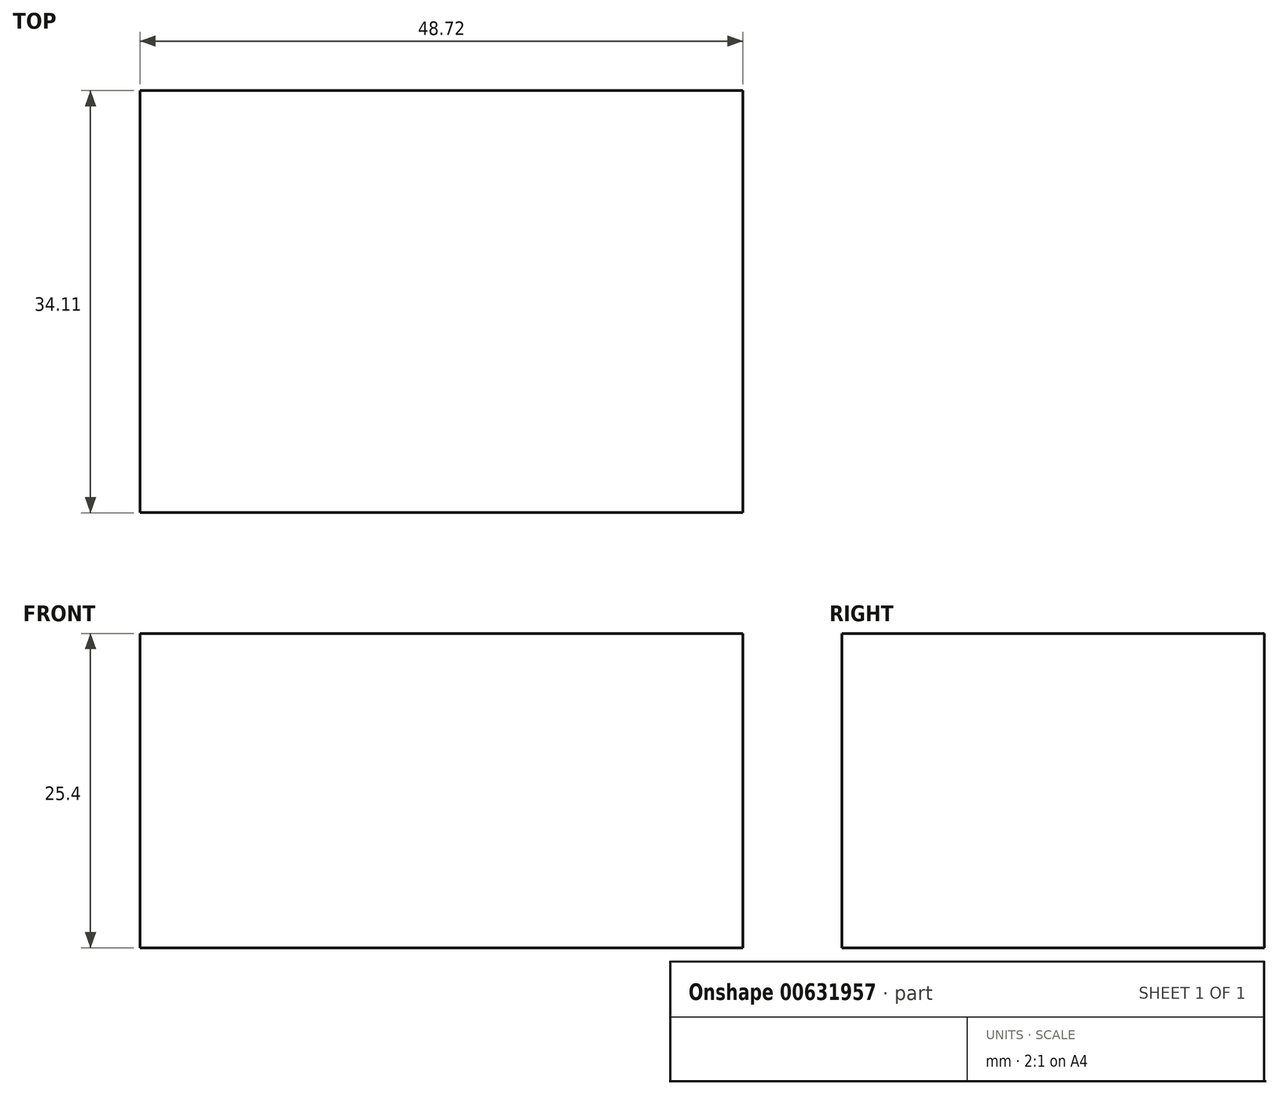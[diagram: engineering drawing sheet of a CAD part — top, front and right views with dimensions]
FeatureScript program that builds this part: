
annotation { "Feature Type Name" : "Feature", "Feature Type Description" : "" }
export const myFeature = defineFeature(function(context is Context, id is Id, definition is map)
    precondition{}
    {
        {
            var Q0;
            Q0=qCreatedBy(makeId("Top.planeOp"),FACE);
            var sketch = newSketch(context, id + "F0", { "sketchPlane" : qUnion([Q0])});
            skLineSegment(sketch, "E0.bottom", {"start": v(-12.86, 21.65) * mm, "end": v(-61.58, 21.65) * mm});
            skLineSegment(sketch, "E0.top", {"start": v(-12.86, 55.76) * mm, "end": v(-61.58, 55.76) * mm});
            skLineSegment(sketch, "E0.left", {"start": v(-12.86, 21.65) * mm, "end": v(-12.86, 55.76) * mm});
            skLineSegment(sketch, "E0.right", {"start": v(-61.58, 21.65) * mm, "end": v(-61.58, 55.76) * mm});
            skPoint(sketch, "E0.middle", {"position": v(-37.22, 38.7) * mm});
            skLineSegment(sketch, "E1.bottom", {"start": v(-42.09, 21.65) * mm, "end": v(16.38, 21.65) * mm});
            skLineSegment(sketch, "E1.top", {"start": v(-42.09, 21.65) * mm, "end": v(16.38, 21.65) * mm});
            skLineSegment(sketch, "E1.left", {"start": v(-42.09, 21.65) * mm, "end": v(-42.09, 21.65) * mm});
            skLineSegment(sketch, "E1.right", {"start": v(16.38, 21.65) * mm, "end": v(16.38, 21.65) * mm});
            skPoint(sketch, "E1.middle", {"position": v(-12.86, 21.65) * mm});
            skSolve(sketch);
        }
        {
            var Q0;
            Q0 = qSketchRegion(id + "F0", true);
            extrude(context, id + "F1", {"entities" : qUnion([Q0]), "depth" : 25.4 * mm, "offsetDistance" : 25.4 * mm});
        }
    });
